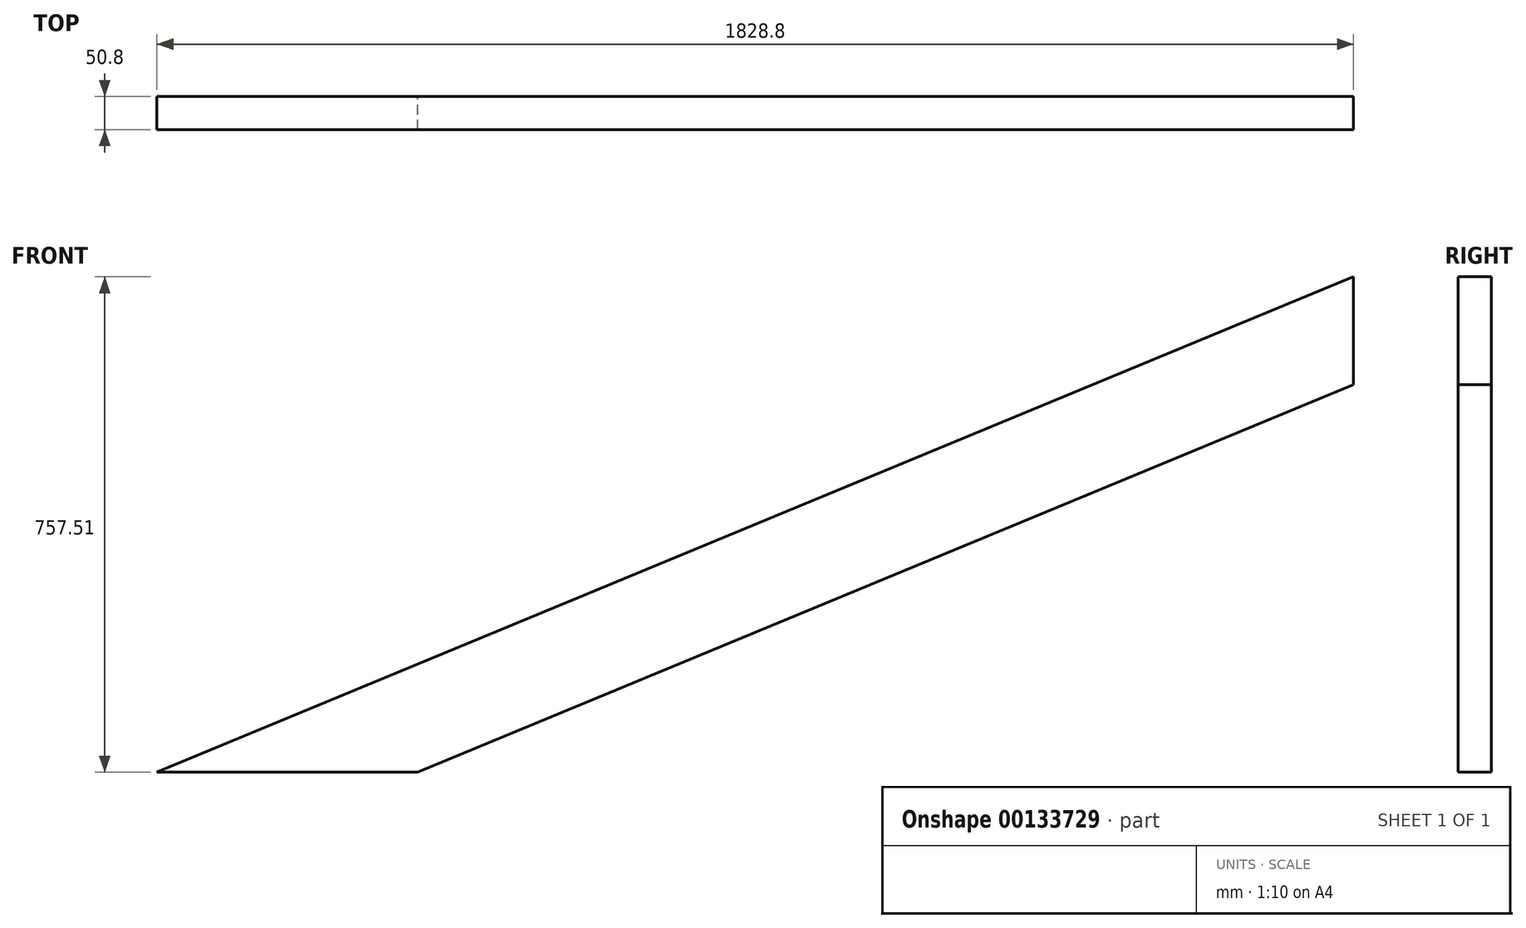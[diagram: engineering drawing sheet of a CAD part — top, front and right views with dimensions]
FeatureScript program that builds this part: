
annotation { "Feature Type Name" : "Feature", "Feature Type Description" : "" }
export const myFeature = defineFeature(function(context is Context, id is Id, definition is map)
    precondition{}
    {
        {
            var Q0;
            Q0=qCreatedBy(makeId("Front.planeOp"),FACE);
            var sketch = newSketch(context, id + "F0", { "sketchPlane" : qUnion([Q0])});
            skLineSegment(sketch, "E0.bottom", {"start": v(0, 0) * mm, "end": v(1828.8, 0) * mm});
            skLineSegment(sketch, "E0.top", {"start": v(0, 757.51) * mm, "end": v(1828.8, 757.51) * mm});
            skLineSegment(sketch, "E0.left", {"start": v(0, 0) * mm, "end": v(0, 757.51) * mm});
            skLineSegment(sketch, "E0.right", {"start": v(1828.8, 0) * mm, "end": v(1828.8, 757.51) * mm});
            skLineSegment(sketch, "E1", {"start": v(0, 0) * mm, "end": v(1828.8, 757.51) * mm});
            skLineSegment(sketch, "E2", {"start": v(0, 0) * mm, "end": v(58.32, -140.8) * mm});
            skLineSegment(sketch, "E3", {"start": v(58.32, -140.8) * mm, "end": v(1490.49, 452.42) * mm});
            skLineSegment(sketch, "E4", {"start": v(1828.8, 757.51) * mm, "end": v(1887.12, 616.71) * mm});
            skLineSegment(sketch, "E5", {"start": v(1490.49, 452.42) * mm, "end": v(1887.12, 616.71) * mm});
            skSolve(sketch);
        }
        {
            var Q0;
            {var subQ5=sQuery(id+"F0.wireOp",EDGE,"E1");Q0=makeQuery(id+"F0.imprint","IMPRINT",FACE,{"disambiguationData":[TD([[makeQuery(id+"F0.imprint","IMPRINT",EDGE,{"derivedFrom":subQ5}),-1.0]])]});}
            extrude(context, id + "F1", {"entities" : qUnion([Q0]), "depth" : 50.8 * mm});
        }
    });
